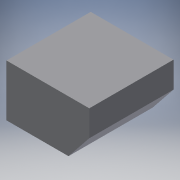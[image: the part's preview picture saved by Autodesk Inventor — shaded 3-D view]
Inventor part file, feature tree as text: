
AUTODESK INVENTOR PART (.ipt)
format: ipt  version: 2017 (Build 210142000, 142)  size: 187,904 bytes
history: native  units: mm
features: extrude x5, sketch x5, reference x4, projected_geometry x4, chamfer x3, other x3, draft x1, shell x1
ambient origin geometry x8: Origin, YZ Plane, XZ Plane, XY Plane, X Axis, Y Axis, Z Axis, Center Point
bodies: Solid1 (feature_tree)
feature tree (26):
  extrude  "Extrusion1"  Depth=3.490659mm
  draft  "FaceDraft1"
  extrude  "Extrusion2"  Depth=44.0mm
  extrude  "Extrusion3"  Depth=73.0mm
  shell  "Shell1"  Thickness=1.5mm
  chamfer  "Chamfer1"  Distance=10.11mm
  chamfer  "Chamfer2"  Distance=9.0mm
  extrude  "Extrusion4"  Depth=2.75mm TaperAngle=45.0deg
  chamfer  "Chamfer3"  Distance=3.5mm
  extrude  "Extrusion5"  Depth=2.75mm TaperAngle=0.0deg
  sketch  "Sketch1"  dims[d0=55.0mm d1=0.0mm d2=3.490659mm]
  sketch  "Sketch2"  dims[d3=53.5mm d4=44.0mm]
  reference  "Reference1"
  reference  "Reference2"
  reference  "Reference3"
  reference  "Reference4"
  sketch  "Sketch3"  dims[d5=23.0mm d6=73.0mm d7=1.5mm d8=10.11mm d9=0.0mm]
  sketch  "Sketch4"  dims[d10=6.5mm d11=9.0mm d12=0.0mm]
  projected_geometry  "Projected Loop1"
  projected_geometry  "Projected Loop2"
  projected_geometry  "Projected Loop3"
  projected_geometry  "Projected Loop4"
  sketch  "Sketch5"  dims[d13=3.0mm d14=2.0mm d15=45.0deg d16=1.0mm d17=2.0mm d18=45.0deg d19=3.5mm d20=9.0mm d21=0.0mm d22=3.0mm d23=2.0mm d24=45.0deg d25=22.0mm d26=2.75mm d27=9.0mm d28=0.0mm]
  parser-record x1  (decoder bookkeeping rows leaked as tree rows — omitted from the tree; the rows remain in map.json)
  other  "Ganymede Node.iam"
  other  "core printed:1"
note: 1 file-system path scrubbed to <path> (originals preserved in map.json)
